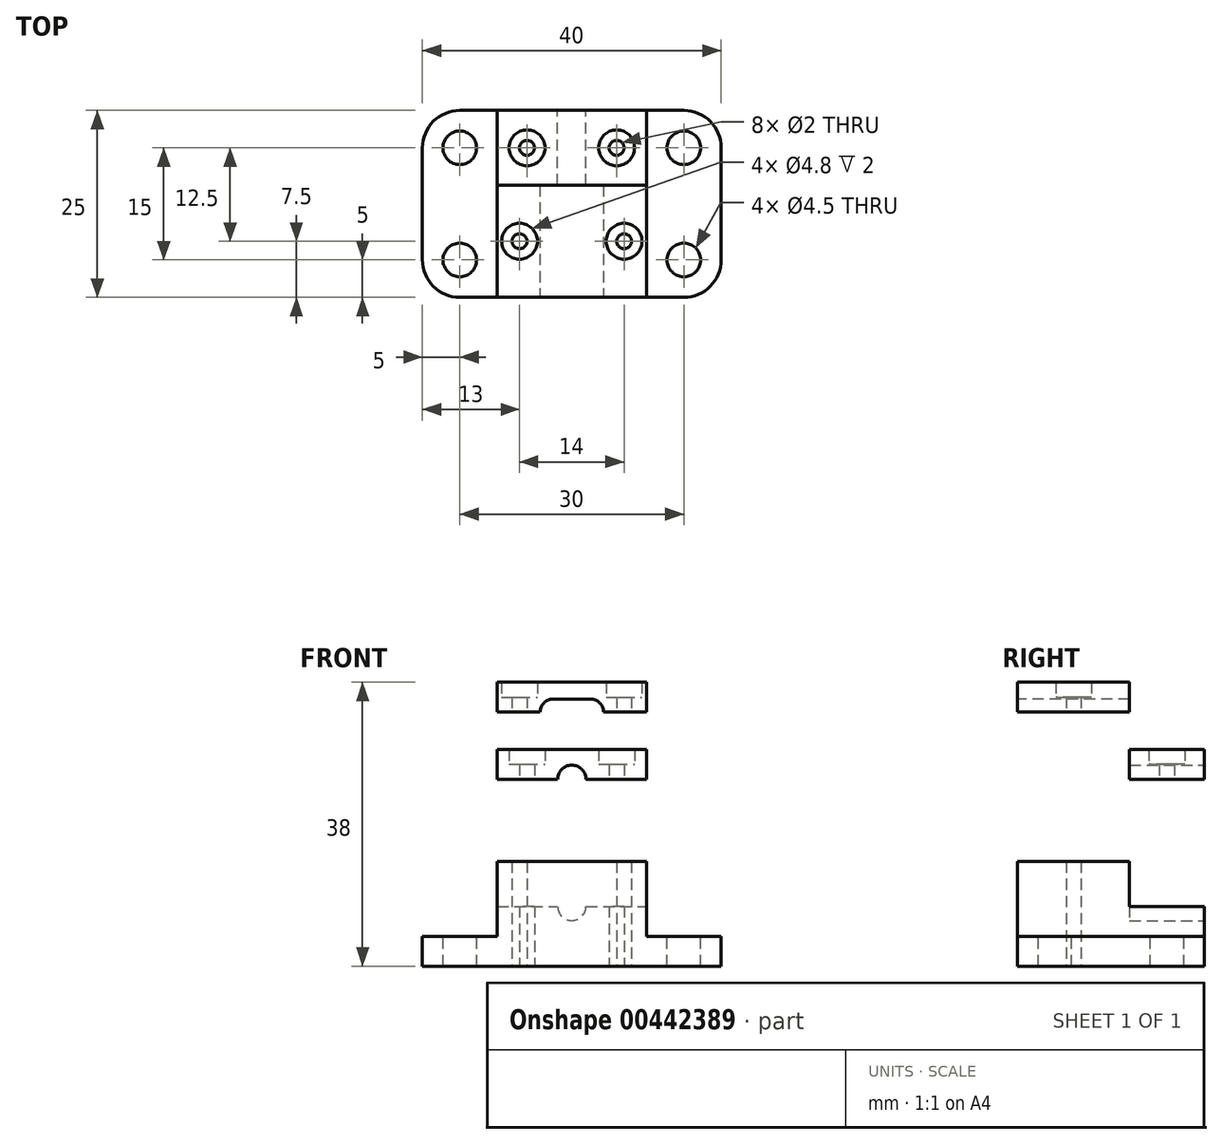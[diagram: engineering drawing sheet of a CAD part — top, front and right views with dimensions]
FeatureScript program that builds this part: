
annotation { "Feature Type Name" : "Feature", "Feature Type Description" : "" }
export const myFeature = defineFeature(function(context is Context, id is Id, definition is map)
    precondition{}
    {
        {
            var Q0;
            Q0=qCreatedBy(makeId("Top.planeOp"),FACE);
            var sketch = newSketch(context, id + "F0", { "sketchPlane" : qUnion([Q0])});
            skLineSegment(sketch, "E0.bottom", {"start": v(20, -12.5) * mm, "end": v(-20, -12.5) * mm});
            skLineSegment(sketch, "E0.top", {"start": v(20, 12.5) * mm, "end": v(-20, 12.5) * mm});
            skLineSegment(sketch, "E0.left", {"start": v(20, -12.5) * mm, "end": v(20, 12.5) * mm});
            skLineSegment(sketch, "E0.right", {"start": v(-20, -12.5) * mm, "end": v(-20, 12.5) * mm});
            skPoint(sketch, "E0.middle", {"position": v(0, 0) * mm});
            skPoint(sketch, "E1", {"position": v(-15, 7.5) * mm});
            skPoint(sketch, "E2.MirrorP", {"position": v(15, 7.5) * mm});
            skPoint(sketch, "E3.MirrorP", {"position": v(-15, -7.5) * mm});
            skPoint(sketch, "E4.MirrorP", {"position": v(15, -7.5) * mm});
            skSolve(sketch);
        }
        {
            var Q0;
            Q0=makeQuery(id+"F0.imprint","IMPRINT",FACE,{"disambiguationData":[TD([[makeQuery(id+"F0.imprint","IMPRINT",EDGE,{"derivedFrom":sQuery(id+"F0.wireOp",EDGE,"E0.bottom")}),-1.0]])]});
            extrude(context, id + "F1", {"entities" : qUnion([Q0]), "depth" : 4 * mm, "offsetDistance" : 25 * mm});
        }
        {
            var Q0;
            Q0=sQuery(id+"F0.wireOp",VERTEX,"E1");
            var Q1;
            Q1=sQuery(id+"F0.wireOp",VERTEX,"E3.MirrorP");
            var Q2;
            Q2=sQuery(id+"F0.wireOp",VERTEX,"E4.MirrorP");
            var Q3;
            Q3=sQuery(id+"F0.wireOp",VERTEX,"E2.MirrorP");
            var Q4;
            Q4=makeQuery(id+"F1.opExtrude","SWEPT_BODY",BODY,{"disambiguationData":[OSD([sQuery(id+"F0.wireOp",EDGE,"E0.bottom"),sQuery(id+"F0.wireOp",EDGE,"E0.top"),sQuery(id+"F0.wireOp",EDGE,"E0.left"),sQuery(id+"F0.wireOp",EDGE,"E0.right")])]});
            hole(context, id + "F2", {"style" : HoleStyle.SIMPLE, "endStyle" : HoleEndStyle.BLIND, "oppositeDirection" : true, "standardTappedOrClearance" : lookupTablePath({ "fit" : "Normal", "standard" : "ISO", "size" : "M4", "type" : "Clearance" }), "standardBlindInLast" : lookupTablePath({ "fit" : "Normal", "standard" : "ISO", "size" : "M4", "type" : "Clearance" }), "holeDiameter" : 4.5 * mm, "majorDiameter" : 5 * mm, "holeDepth" : 50 * mm, "isTappedThrough" : true, "tappedDepth" : 12 * mm, "tapClearance" : 3, "locations" : qUnion([Q0, Q1, Q2, Q3]), "scope" : qUnion([Q4])});
        }
        {
            var Q0;
            Q0=makeQuery(id+"F1.opExtrude","CAP_FACE",FACE,{"disambiguationData":[OSD([sQuery(id+"F0.wireOp",EDGE,"E0.bottom"),sQuery(id+"F0.wireOp",EDGE,"E0.top"),sQuery(id+"F0.wireOp",EDGE,"E0.left"),sQuery(id+"F0.wireOp",EDGE,"E0.right")])],"isStart":false});
            var sketch = newSketch(context, id + "F3", { "sketchPlane" : qUnion([Q0])});
            skLineSegment(sketch, "E5.bottom", {"start": v(10, -12.5) * mm, "end": v(-10, -12.5) * mm});
            skLineSegment(sketch, "E5.top", {"start": v(10, 12.5) * mm, "end": v(-10, 12.5) * mm});
            skLineSegment(sketch, "E5.left", {"start": v(10, -12.5) * mm, "end": v(10, 12.5) * mm});
            skLineSegment(sketch, "E5.right", {"start": v(-10, -12.5) * mm, "end": v(-10, 12.5) * mm});
            skPoint(sketch, "E5.middle", {"position": v(0, 0) * mm});
            skSolve(sketch);
        }
        {
            var Q0;
            Q0 = qSketchRegion(id + "F3", true);
            extrude(context, id + "F4", {"entities" : qUnion([Q0]), "operationType" : NewBodyOperationType.ADD, "depth" : 10 * mm, "offsetDistance" : 25 * mm});
        }
        {
            var Q0;
            Q0=makeQuery(id+"F4.boolean.opBoolean","MERGE",FACE,{"derivedFrom":[makeQuery(id+"F1.opExtrude","SWEPT_FACE",FACE,{"disambiguationData":[OSD([sQuery(id+"F0.wireOp",EDGE,"E0.top")])]}),makeQuery(id+"F4.opExtrude","SWEPT_FACE",FACE,{"disambiguationData":[OSD([sQuery(id+"F3.wireOp",EDGE,"E5.top")])]})]});
            var sketch = newSketch(context, id + "F5", { "sketchPlane" : qUnion([Q0])});
            skCircle(sketch, "E6", {"center": v(0, 8) * mm, "radius": 1.9 * mm});
            skLineSegment(sketch, "E7.bottom", {"start": v(10, 14) * mm, "end": v(-10, 14) * mm});
            skLineSegment(sketch, "E7.top", {"start": v(10, 8) * mm, "end": v(-10, 8) * mm});
            skLineSegment(sketch, "E7.left", {"start": v(10, 14) * mm, "end": v(10, 8) * mm});
            skLineSegment(sketch, "E7.right", {"start": v(-10, 14) * mm, "end": v(-10, 8) * mm});
            skSolve(sketch);
        }
        {
            var Q0;
            Q0=makeQuery(id+"F5.imprint","IMPRINT",FACE,{"disambiguationData":[TD([[makeQuery(id+"F5.imprint","IMPRINT",EDGE,{"derivedFrom":sQuery(id+"F5.wireOp",EDGE,"E7.bottom")}),-1.0]])]});
            var Q1;
            {var subQ0=sQuery(id+"F5.wireOp",EDGE,"E7.top");var subQ1=sQuery(id+"F5.wireOp",EDGE,"E6");var subQ2=makeQuery(id+"F5.imprint","INTERSECT",VERTEX,{"disambiguationData":[OD(0.0)],"derivedFrom":[subQ1,subQ0]});Q1=makeQuery(id+"F5.imprint","IMPRINT",FACE,{"disambiguationData":[TD([[makeQuery(id+"F5.imprint","IMPRINT",EDGE,{"disambiguationData":[TD([[subQ2,-1.0]])],"derivedFrom":subQ1}),1.0]])]});}
            var Q2;
            {var subQ0=sQuery(id+"F5.wireOp",EDGE,"E7.top");var subQ1=sQuery(id+"F5.wireOp",EDGE,"E6");var subQ2=makeQuery(id+"F5.imprint","INTERSECT",VERTEX,{"disambiguationData":[OD(0.0)],"derivedFrom":[subQ1,subQ0]});Q2=makeQuery(id+"F5.imprint","IMPRINT",FACE,{"disambiguationData":[TD([[makeQuery(id+"F5.imprint","IMPRINT",EDGE,{"disambiguationData":[TD([[subQ2,1.0]])],"derivedFrom":subQ1}),1.0]])]});}
            extrude(context, id + "F6", {"entities" : qUnion([Q0, Q1, Q2]), "operationType" : NewBodyOperationType.REMOVE, "oppositeDirection" : true, "depth" : 10 * mm, "offsetDistance" : 25 * mm});
        }
        {
            var Q0;
            Q0=qCreatedBy(makeId("Top.planeOp"),FACE);
            cPlane(context, id + "F7", {"entities" : qUnion([Q0]), "cplaneType" : CPlaneType.OFFSET, "offset" : 25 * mm, "width" : 150 * mm, "height" : 150 * mm});
        }
        {
            var Q0;
            Q0=qCreatedBy(id+"F7.planeOp",FACE);
            var sketch = newSketch(context, id + "F8", { "sketchPlane" : qUnion([Q0])});
            skLineSegment(sketch, "E8.bottom", {"start": v(-10, 2.5) * mm, "end": v(10, 2.5) * mm});
            skLineSegment(sketch, "E8.top", {"start": v(-10, 12.5) * mm, "end": v(10, 12.5) * mm});
            skLineSegment(sketch, "E8.left", {"start": v(-10, 2.5) * mm, "end": v(-10, 12.5) * mm});
            skLineSegment(sketch, "E8.right", {"start": v(10, 2.5) * mm, "end": v(10, 12.5) * mm});
            skSolve(sketch);
        }
        {
            var Q0;
            Q0 = qSketchRegion(id + "F8", true);
            extrude(context, id + "F9", {"entities" : qUnion([Q0]), "depth" : 4 * mm, "offsetDistance" : 25 * mm});
        }
        {
            var Q0;
            Q0=makeQuery(id+"F9.opExtrude","SWEPT_FACE",FACE,{"disambiguationData":[OSD([sQuery(id+"F8.wireOp",EDGE,"E8.top")])]});
            var sketch = newSketch(context, id + "F10", { "sketchPlane" : qUnion([Q0])});
            skCircle(sketch, "E9", {"center": v(0, 25) * mm, "radius": 1.9 * mm});
            skSolve(sketch);
        }
        {
            var Q0;
            Q0 = qSketchRegion(id + "F10", true);
            var Q1;
            Q1=makeQuery(id+"F9.opExtrude","SWEPT_FACE",FACE,{"disambiguationData":[OSD([sQuery(id+"F8.wireOp",EDGE,"E8.bottom")])]});
            extrude(context, id + "F11", {"entities" : qUnion([Q0]), "operationType" : NewBodyOperationType.REMOVE, "endBound" : BoundingType.UP_TO_SURFACE, "oppositeDirection" : true, "depth" : 25 * mm, "endBoundEntityFace" : qUnion([Q1]), "offsetDistance" : 25 * mm});
        }
        {
            var Q0;
            Q0=makeQuery(id+"F9.opExtrude","CAP_FACE",FACE,{"disambiguationData":[OSD([sQuery(id+"F8.wireOp",EDGE,"E8.bottom"),sQuery(id+"F8.wireOp",EDGE,"E8.top"),sQuery(id+"F8.wireOp",EDGE,"E8.left"),sQuery(id+"F8.wireOp",EDGE,"E8.right")])],"isStart":false});
            var sketch = newSketch(context, id + "F12", { "sketchPlane" : qUnion([Q0])});
            skPoint(sketch, "E10", {"position": v(-6, 7.5) * mm});
            skPoint(sketch, "E10.positionSnap0", {"position": v(-10, 7.5) * mm});
            skPoint(sketch, "E11.MirrorP", {"position": v(6, 7.5) * mm});
            skSolve(sketch);
        }
        {
            var Q0;
            Q0=sQuery(id+"F12.wireOp",VERTEX,"E10");
            var Q1;
            Q1=sQuery(id+"F12.wireOp",VERTEX,"E11.MirrorP");
            var Q2;
            Q2=makeQuery(id+"F1.opExtrude","SWEPT_BODY",BODY,{"disambiguationData":[OSD([sQuery(id+"F0.wireOp",EDGE,"E0.bottom"),sQuery(id+"F0.wireOp",EDGE,"E0.top"),sQuery(id+"F0.wireOp",EDGE,"E0.left"),sQuery(id+"F0.wireOp",EDGE,"E0.right")])]});
            var Q3;
            Q3=makeQuery(id+"F9.opExtrude","SWEPT_BODY",BODY,{"disambiguationData":[OSD([sQuery(id+"F8.wireOp",EDGE,"E8.bottom"),sQuery(id+"F8.wireOp",EDGE,"E8.top"),sQuery(id+"F8.wireOp",EDGE,"E8.left"),sQuery(id+"F8.wireOp",EDGE,"E8.right")])]});
            hole(context, id + "F13", {"style" : HoleStyle.C_BORE, "endStyle" : HoleEndStyle.BLIND, "holeDiameter" : 2 * mm, "cBoreDiameter" : 4.8 * mm, "cBoreDepth" : 2 * mm, "majorDiameter" : 5 * mm, "holeDepth" : 50 * mm, "isTappedThrough" : true, "tappedDepth" : 12 * mm, "tapClearance" : 3, "locations" : qUnion([Q0, Q1]), "scope" : qUnion([Q2, Q3])});
        }
        {
            var Q0;
            Q0=makeQuery(id+"F4.opExtrude","CAP_FACE",FACE,{"disambiguationData":[OSD([sQuery(id+"F3.wireOp",EDGE,"E5.bottom"),sQuery(id+"F3.wireOp",EDGE,"E5.top"),sQuery(id+"F3.wireOp",EDGE,"E5.left"),sQuery(id+"F3.wireOp",EDGE,"E5.right")])],"isStart":false});
            cPlane(context, id + "F14", {"entities" : qUnion([Q0]), "cplaneType" : CPlaneType.OFFSET, "offset" : 20 * mm, "width" : 150 * mm, "height" : 150 * mm});
        }
        {
            var Q0;
            Q0=qCreatedBy(id+"F14.planeOp",FACE);
            var sketch = newSketch(context, id + "F15", { "sketchPlane" : qUnion([Q0])});
            skLineSegment(sketch, "E12.bottom", {"start": v(-10, -12.5) * mm, "end": v(10, -12.5) * mm});
            skLineSegment(sketch, "E12.top", {"start": v(-10, 2.5) * mm, "end": v(10, 2.5) * mm});
            skLineSegment(sketch, "E12.left", {"start": v(-10, -12.5) * mm, "end": v(-10, 2.5) * mm});
            skLineSegment(sketch, "E12.right", {"start": v(10, -12.5) * mm, "end": v(10, 2.5) * mm});
            skPoint(sketch, "E13.positionSnap0", {"position": v(-10, -5) * mm});
            skSolve(sketch);
        }
        {
            var Q0;
            Q0=makeQuery(id+"F15.imprint","IMPRINT",FACE,{"disambiguationData":[TD([[makeQuery(id+"F15.imprint","IMPRINT",EDGE,{"derivedFrom":sQuery(id+"F15.wireOp",EDGE,"E12.bottom")}),1.0]])]});
            extrude(context, id + "F16", {"entities" : qUnion([Q0]), "depth" : 4 * mm, "offsetDistance" : 25 * mm});
        }
        {
            var Q0;
            Q0=makeQuery(id+"F16.opExtrude","SWEPT_FACE",FACE,{"disambiguationData":[OSD([sQuery(id+"F15.wireOp",EDGE,"E12.bottom")])]});
            var sketch = newSketch(context, id + "F17", { "sketchPlane" : qUnion([Q0])});
            skLineSegment(sketch, "E14", {"start": v(-2.5, 34) * mm, "end": v(2.5, 34) * mm, "construction": true});
            skArc(sketch, "E15.0.startCap", {"start": v(-2.5, 32.25) * mm, "mid": v(-4.25, 34) * mm, "end": v(-2.5, 35.75) * mm});
            skArc(sketch, "E15.0.endCap", {"start": v(2.5, 35.75) * mm, "mid": v(4.25, 34) * mm, "end": v(2.5, 32.25) * mm});
            skLineSegment(sketch, "E15.0.left", {"start": v(-2.5, 35.75) * mm, "end": v(2.5, 35.75) * mm});
            skLineSegment(sketch, "E15.0.right", {"start": v(-2.5, 32.25) * mm, "end": v(2.5, 32.25) * mm});
            skLineSegment(sketch, "E16", {"start": v(-2.5, 14) * mm, "end": v(2.5, 14) * mm, "construction": true});
            skArc(sketch, "E17.0.startCap", {"start": v(-2.5, 12.25) * mm, "mid": v(-4.25, 14) * mm, "end": v(-2.5, 15.75) * mm});
            skArc(sketch, "E17.0.endCap", {"start": v(2.5, 15.75) * mm, "mid": v(4.25, 14) * mm, "end": v(2.5, 12.25) * mm});
            skLineSegment(sketch, "E17.0.left", {"start": v(-2.5, 15.75) * mm, "end": v(2.5, 15.75) * mm});
            skLineSegment(sketch, "E17.0.right", {"start": v(-2.5, 12.25) * mm, "end": v(2.5, 12.25) * mm});
            skSolve(sketch);
        }
        {
            var Q0;
            {var subQ0=sQuery(id+"F17.wireOp",EDGE,"E15.0.left");Q0=makeQuery(id+"F17.imprint","IMPRINT",FACE,{"disambiguationData":[TD([[makeQuery(id+"F17.imprint","IMPRINT",EDGE,{"derivedFrom":subQ0}),-1.0]])]});}
            var Q1;
            Q1=makeQuery(id+"F17.imprint","IMPRINT",FACE,{"disambiguationData":[TD([[makeQuery(id+"F17.imprint","IMPRINT",EDGE,{"derivedFrom":sQuery(id+"F17.wireOp",EDGE,"E17.0.startCap")}),-1.0]])]});
            extrude(context, id + "F18", {"entities" : qUnion([Q0, Q1]), "operationType" : NewBodyOperationType.REMOVE, "oppositeDirection" : true, "depth" : 25 * mm, "offsetDistance" : 25 * mm});
        }
        {
            var Q0;
            Q0=makeQuery(id+"F16.opExtrude","CAP_FACE",FACE,{"disambiguationData":[OSD([sQuery(id+"F15.wireOp",EDGE,"E12.bottom"),sQuery(id+"F15.wireOp",EDGE,"E12.top"),sQuery(id+"F15.wireOp",EDGE,"E12.left"),sQuery(id+"F15.wireOp",EDGE,"E12.right")])],"isStart":false});
            var sketch = newSketch(context, id + "F19", { "sketchPlane" : qUnion([Q0])});
            skPoint(sketch, "E18", {"position": v(-7, -5) * mm});
            skPoint(sketch, "E19", {"position": v(-10, -5) * mm});
            skPoint(sketch, "E20.MirrorP", {"position": v(7, -5) * mm});
            skSolve(sketch);
        }
        {
            var Q0;
            Q0=sQuery(id+"F19.wireOp",VERTEX,"E18");
            var Q1;
            Q1=sQuery(id+"F19.wireOp",VERTEX,"E20.MirrorP");
            var Q2;
            Q2=makeQuery(id+"F1.opExtrude","SWEPT_BODY",BODY,{"disambiguationData":[OSD([sQuery(id+"F0.wireOp",EDGE,"E0.bottom"),sQuery(id+"F0.wireOp",EDGE,"E0.top"),sQuery(id+"F0.wireOp",EDGE,"E0.left"),sQuery(id+"F0.wireOp",EDGE,"E0.right")])]});
            var Q3;
            Q3=makeQuery(id+"F16.opExtrude","SWEPT_BODY",BODY,{"disambiguationData":[OSD([sQuery(id+"F15.wireOp",EDGE,"E12.bottom"),sQuery(id+"F15.wireOp",EDGE,"E12.top"),sQuery(id+"F15.wireOp",EDGE,"E12.left"),sQuery(id+"F15.wireOp",EDGE,"E12.right")])]});
            hole(context, id + "F20", {"style" : HoleStyle.C_BORE, "endStyle" : HoleEndStyle.BLIND, "holeDiameter" : 2 * mm, "cBoreDiameter" : 4.8 * mm, "cBoreDepth" : 2 * mm, "majorDiameter" : 5 * mm, "holeDepth" : 50 * mm, "isTappedThrough" : true, "tappedDepth" : 12 * mm, "tapClearance" : 3, "locations" : qUnion([Q0, Q1]), "scope" : qUnion([Q2, Q3])});
        }
        {
            var Q0;
            Q0=makeQuery(id+"F1.opExtrude","SWEPT_EDGE",EDGE,{"disambiguationData":[OSD([sQuery(id+"F0.wireOp",EDGE,"E0.top"),sQuery(id+"F0.wireOp",EDGE,"E0.right")])]});
            var Q1;
            Q1=makeQuery(id+"F1.opExtrude","SWEPT_EDGE",EDGE,{"disambiguationData":[OSD([sQuery(id+"F0.wireOp",EDGE,"E0.bottom"),sQuery(id+"F0.wireOp",EDGE,"E0.right")])]});
            var Q2;
            Q2=makeQuery(id+"F1.opExtrude","SWEPT_EDGE",EDGE,{"disambiguationData":[OSD([sQuery(id+"F0.wireOp",EDGE,"E0.bottom"),sQuery(id+"F0.wireOp",EDGE,"E0.left")])]});
            var Q3;
            Q3=makeQuery(id+"F1.opExtrude","SWEPT_EDGE",EDGE,{"disambiguationData":[OSD([sQuery(id+"F0.wireOp",EDGE,"E0.top"),sQuery(id+"F0.wireOp",EDGE,"E0.left")])]});
            fillet(context, id + "F21", {"entities" : qUnion([Q0, Q1, Q2, Q3]), "radius" : 5 * mm, "tangentPropagation" : true, "allowEdgeOverflow" : false});
        }
    });
